# Revit family: Urinal-Waterless-Sloan-WES-7000_Series
name_source: partatom
category: Plumbing Fixtures
revit_build: Autodesk Revit 2014 (Build: 20130308_1515(x64)
units: mm (PartAtom-declared; Revit-internal decimal feet)

## types (2) — shared parameters
ADA Compliant = Yes
Assembly Code = D2010210
CW Connection = No
Default Elevation = 24"
Fixture Color = White
Flush Choice = Waterfree
Flush Volume(s)/Flow Rate(s) = Waterfree
HW Connection = No
High Efficiency = Yes
Manufacturer = Sloan
Material = Vitreous China-Sloan-White
Mounting = Wall Hung
Price = Prices may vary. Please consult Sloan Rep for most up-to-date price list.
Product Documentation Link = https://specifications.sloan.com
Product Page URL = https://www.sloan.com
Revised Date = 9/30/2016
Spud Location = Not Applicable
URL = www.sloan.com
Vent Connection = No
Warranty = 3 Year (Limited)
Waste Connection = Yes
zero-valued in all types: CWFU, HWFU, WFU

## per-type parameters (varying)
| type | Description | Order Code |
| WES-7000 | Wall hung, wall outlet, Waterfree Vitreous China Urinal | 1007000 |
| WES-7000-STG | Wall hung, wall outlet, Waterfree Vitreous China Urinal with SloanTec™ Hydrophobic, antimicrobial glaze | 1077000 |

note: column(s) folded — value = type name in every type: Model

## geometry (parser evidence)
native form markers: Sweep x3
no freeform markers — native parametric forms only
